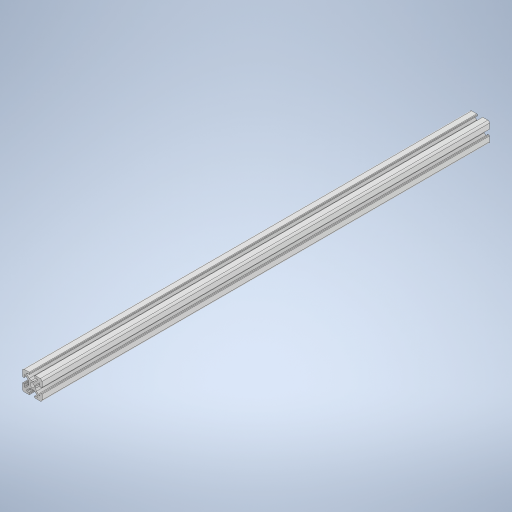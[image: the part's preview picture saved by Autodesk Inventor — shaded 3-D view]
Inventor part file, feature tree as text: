
AUTODESK INVENTOR PART (.ipt)
format: ipt  version: 2023 (Build 270158000, 158)  size: 325,632 bytes
history: mixed  units: in
note: dims shown in document units (in); Inventor stores cm internally (conversion verified against a paired STEP export)
features: mirror x1, imported_body x1
ambient origin geometry x8: Origin, YZ Plane, XZ Plane, XY Plane, X Axis, Y Axis, Z Axis, Center Point
bodies: Solid1 (imported_parasolid)
feature tree (2):
  mirror  "Mirror2"
  imported_body  NMx_Import_Brep_tag  [imported B-rep: ~75 faces, bbox_mm=[20.0, 20.0, 457.2]]
